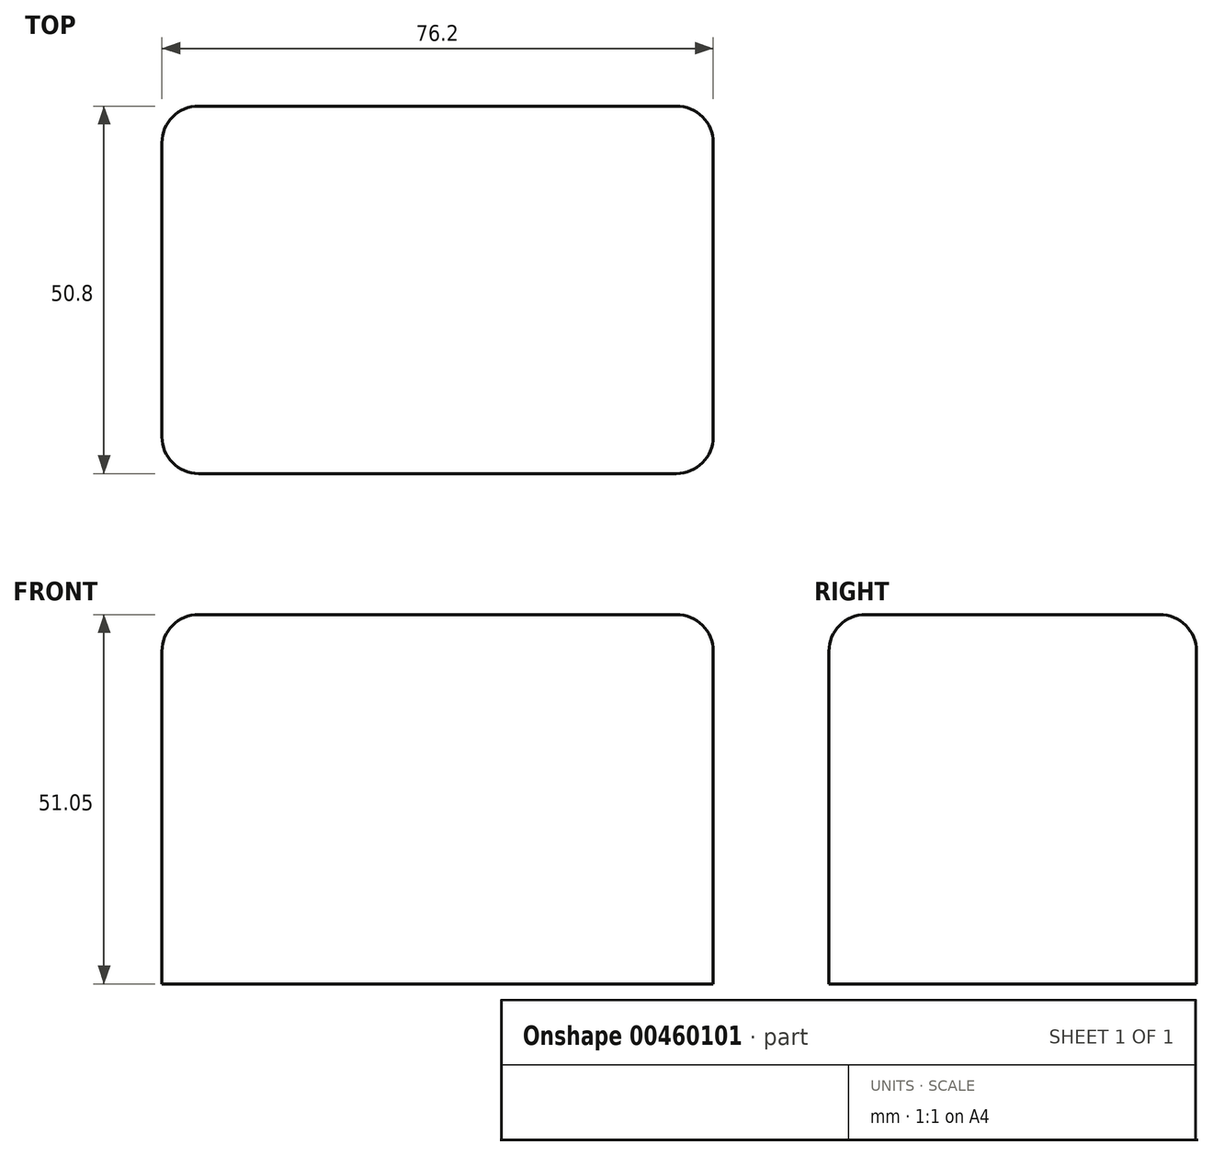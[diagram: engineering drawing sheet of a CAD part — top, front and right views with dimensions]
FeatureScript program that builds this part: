
annotation { "Feature Type Name" : "Feature", "Feature Type Description" : "" }
export const myFeature = defineFeature(function(context is Context, id is Id, definition is map)
    precondition{}
    {
        {
            var Q0;
            Q0=qCreatedBy(makeId("Top.planeOp"),FACE);
            var sketch = newSketch(context, id + "F0", { "sketchPlane" : qUnion([Q0])});
            skLineSegment(sketch, "E0.bottom", {"start": v(-45.25, 24.97) * mm, "end": v(30.95, 24.97) * mm});
            skLineSegment(sketch, "E0.top", {"start": v(-45.25, -25.83) * mm, "end": v(30.95, -25.83) * mm});
            skLineSegment(sketch, "E0.left", {"start": v(-45.25, 24.97) * mm, "end": v(-45.25, -25.83) * mm});
            skLineSegment(sketch, "E0.right", {"start": v(30.95, 24.97) * mm, "end": v(30.95, -25.83) * mm});
            skSolve(sketch);
        }
        {
            var Q0;
            Q0=makeQuery(id+"F0.imprint","IMPRINT",FACE,{"disambiguationData":[TD([[makeQuery(id+"F0.imprint","IMPRINT",EDGE,{"derivedFrom":sQuery(id+"F0.wireOp",EDGE,"E0.bottom")}),-1.0]])]});
            extrude(context, id + "F1", {"entities" : qUnion([Q0]), "depth" : 51.05 * mm});
        }
        {
            var Q0;
            Q0=makeQuery(id+"F1.opExtrude","CAP_FACE",FACE,{"disambiguationData":[OSD([sQuery(id+"F0.wireOp",EDGE,"E0.bottom"),sQuery(id+"F0.wireOp",EDGE,"E0.top"),sQuery(id+"F0.wireOp",EDGE,"E0.left"),sQuery(id+"F0.wireOp",EDGE,"E0.right")])],"isStart":false});
            fillet(context, id + "F2", {"entities" : qUnion([Q0]), "radius" : 5.08 * mm, "tangentPropagation" : true, "allowEdgeOverflow" : false});
        }
        {
            var Q0;
            Q0=makeQuery(id+"F1.opExtrude","SWEPT_EDGE",EDGE,{"disambiguationData":[OSD([sQuery(id+"F0.wireOp",EDGE,"E0.bottom"),sQuery(id+"F0.wireOp",EDGE,"E0.left")])]});
            var Q1;
            Q1=makeQuery(id+"F1.opExtrude","SWEPT_EDGE",EDGE,{"disambiguationData":[OSD([sQuery(id+"F0.wireOp",EDGE,"E0.top"),sQuery(id+"F0.wireOp",EDGE,"E0.left")])]});
            var Q2;
            Q2=makeQuery(id+"F1.opExtrude","SWEPT_EDGE",EDGE,{"disambiguationData":[OSD([sQuery(id+"F0.wireOp",EDGE,"E0.top"),sQuery(id+"F0.wireOp",EDGE,"E0.right")])]});
            var Q3;
            Q3=makeQuery(id+"F1.opExtrude","SWEPT_EDGE",EDGE,{"disambiguationData":[OSD([sQuery(id+"F0.wireOp",EDGE,"E0.bottom"),sQuery(id+"F0.wireOp",EDGE,"E0.right")])]});
            fillet(context, id + "F3", {"entities" : qUnion([Q0, Q1, Q2, Q3]), "radius" : 5.08 * mm, "tangentPropagation" : true, "allowEdgeOverflow" : false});
        }
    });
